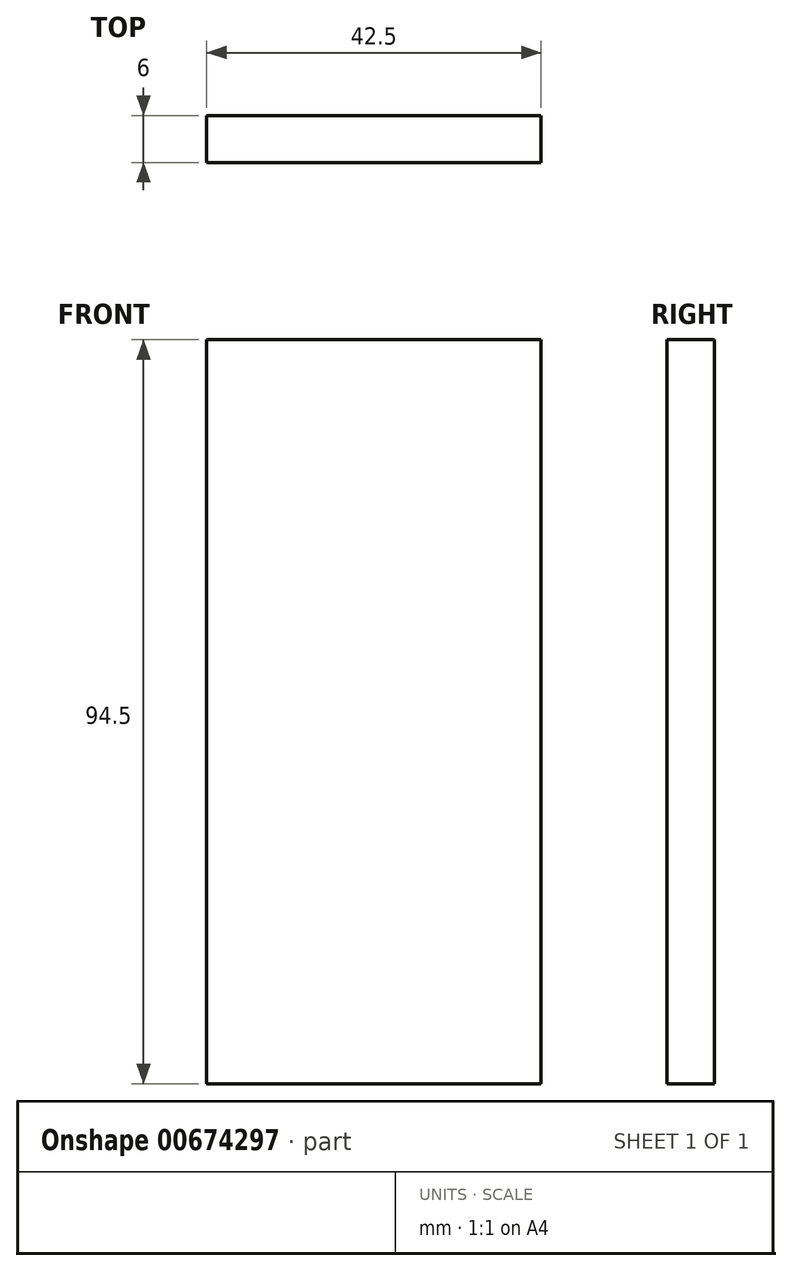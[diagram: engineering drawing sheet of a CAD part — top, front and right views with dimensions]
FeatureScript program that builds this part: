
annotation { "Feature Type Name" : "Feature", "Feature Type Description" : "" }
export const myFeature = defineFeature(function(context is Context, id is Id, definition is map)
    precondition{}
    {
        {
            var Q0;
            Q0=qCreatedBy(makeId("Front.planeOp"),FACE);
            var sketch = newSketch(context, id + "F0", { "sketchPlane" : qUnion([Q0])});
            skLineSegment(sketch, "E0.bottom", {"start": v(-22.95, 45.06) * mm, "end": v(19.55, 45.06) * mm});
            skLineSegment(sketch, "E0.top", {"start": v(-22.95, -49.44) * mm, "end": v(19.55, -49.44) * mm});
            skLineSegment(sketch, "E0.left", {"start": v(-22.95, 45.06) * mm, "end": v(-22.95, -49.44) * mm});
            skLineSegment(sketch, "E0.right", {"start": v(19.55, 45.06) * mm, "end": v(19.55, -49.44) * mm});
            skSolve(sketch);
        }
        {
            var Q0;
            Q0 = qSketchRegion(id + "F0", true);
            extrude(context, id + "F1", {"entities" : qUnion([Q0]), "depth" : 6 * mm, "offsetDistance" : 25 * mm});
        }
    });
